SOLIDWORKS PART (.sldprt)
format: sldprt  version: not decoded by parser v0  size: 76,800 bytes
history: native  units: mm
features: plane x3, sketch x3, extrude x3, material x1 (+13 scaffold rows collapsed)
feature tree (23):
  scaffold x13  (default folders/planes/origin — collapsed)
  material  "材质 <未指定>"
  plane  "前视基准面"
  plane  "上视基准面"
  plane  "右视基准面"
  sketch  "草图1"
  extrude  "凸台-拉伸1"  Depth=2mm
  sketch  "草图2"  dims[D1=~1.992132mm]
  extrude  "凸台-拉伸2"  Depth=2mm
  sketch  "草图3"  dims[D1=~3.29906mm]
  extrude  "凸台-拉伸4"  Depth=15mm
decode coverage: 5 of 6 modeling features carry decoded parameters
note: ~ marks probable driven/reference dimensions
note: suppression state not decoded; provenance and decode notes live in map.json
